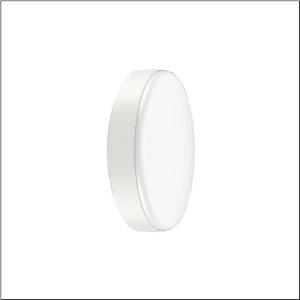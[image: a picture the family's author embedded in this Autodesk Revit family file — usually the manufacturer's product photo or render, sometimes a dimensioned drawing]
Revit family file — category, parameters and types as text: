
# Revit family: round_31_51wc10db34as
name_source: partatom
category: Lighting Fixtures
units: mm (PartAtom-declared; Revit-internal decimal feet)

## family parameters
Cut with Voids When Loaded = No
Host = Face
Light Source = No
Part Type = Normal
Room Calculation Point = No
Round Connector Dimension = Use Diameter
Shared = No

## types (1)
- Round 31 (1 x LED, 4250 lm, 35.4 W, 3000K)
    Apparent Load = 35 VA
    CIE Flux Codes = 44 75 94 94 100
    Color Rendering = 80
    Color Temperature = 3000K
    Default Elevation = 1800 mm
    Description = Round 31, wall and ceiling luminaire, primary optical cover: cover, of PC, opal, light emission: direct distribution, primary light characteristic: symmetric, installation type: surface-mounted, LED, rated luminous flux: 4.250lm, luminous efficacy: 120lm/W, light colour: 830, colour temperature: 3000K, control gear: DALI 2, with terminal, 5-pole, max. 2.5mm², mains connection: 220..240V, AC, 50/60Hz, rated input power: 35.5W, luminaire housing, of PC, traffic white (RAL 9016), diameter: 480mm, brightness and presence sensor, HF sensor, protection rating (complete): IP65, insulation class (complete): insulation class II (safety insulation), certification: CE, impact resistance: IK10, permissible operating ambient temperature: -20..+40°C, permissible storage temperature: -20..+60°C, packaging unit: 1 piece
    Height = 97 mm
    Lamp = 1 x LED
    Lamp Light Flux = 4250 lm
    Lamp Power = 35.4 W
    Lamp count = 1
    Length = 480 mm
    Luminous efficacy = 120 lm/W
    Manufacturer = Siteco
    ModVariant = No
    Model = 51WC10DB34AS
    Mounting Place = Wall
    Mounting Type = Surface mounted
    Number of Poles = 1
    OnlyDefault = Yes
    Power Factor = 1
    Product Name = Round 31
    Product group = wall and ceiling luminaire
    ProductGroupID = 2001
    Protection Class = Protection class II
    Protection Degree = IP 65
    RLX_Detail_Level = 1
    RLX_Emergency_Light_Flux = 0 lm
    RLX_Emergency_Type = 0
    RLX_Emergency_Type_DB = No
    RlxData = <blob elided: 40897 chars, md5=b8b09ff8>
    Socket = socket
    Standby Power = 0 W
    System Light Flux = 4250 lm
    System Power = 35 W
    Type Comments = Product without accessories
    Type Image = l_1007188.jpg
    URL = http://relux.com
    VarID = ---
    Voltage = 0 V
    Weight = 0.00 kg
    Width = 0 mm  [stored 0 ft]

note: [stored X ft] marks values corroborated as IEEE doubles in the binary element streams (Revit-internal decimal feet)

## geometry (parser evidence)
native form markers: Blend x4, Sweep x14
no freeform markers — native parametric forms only
